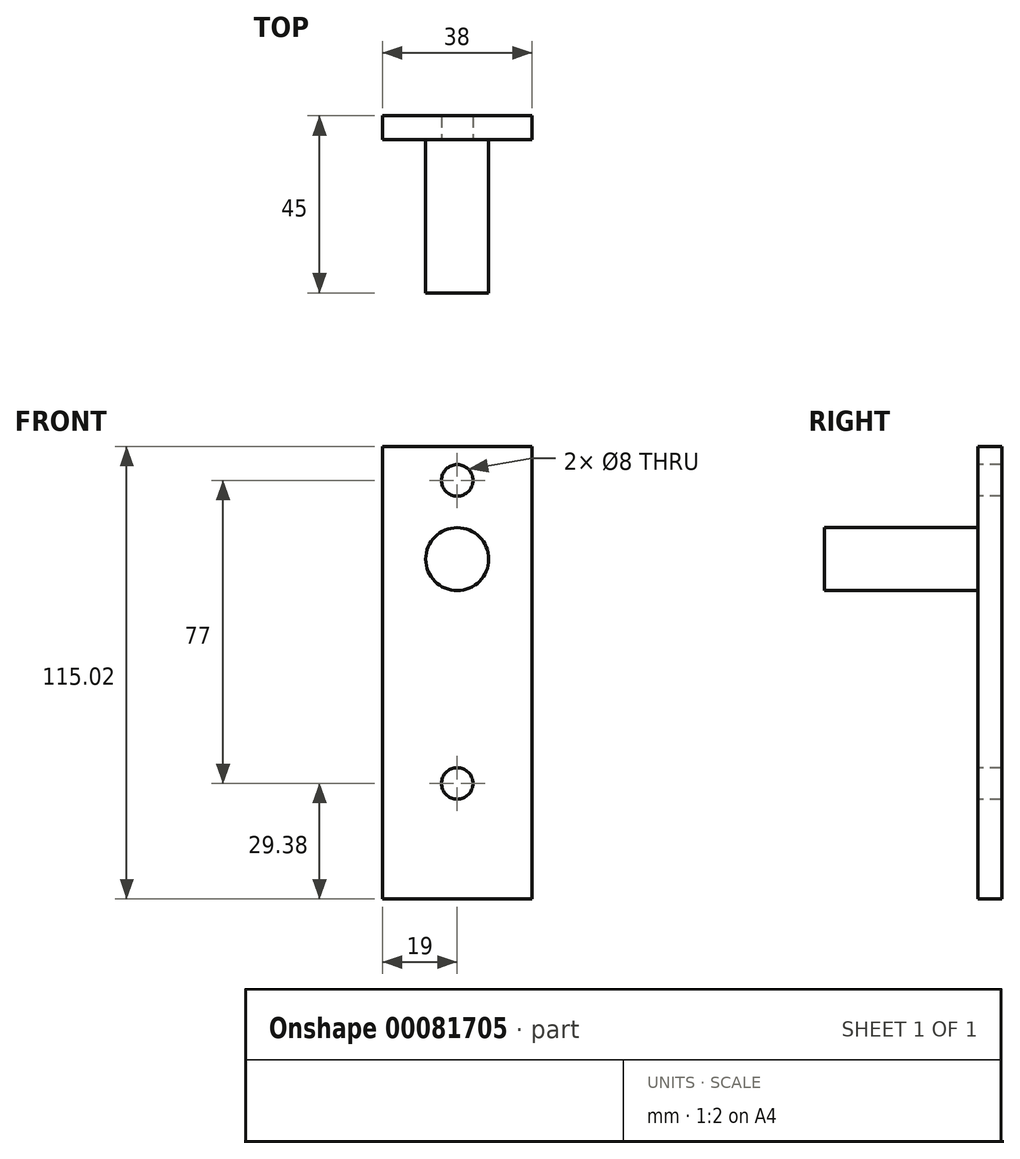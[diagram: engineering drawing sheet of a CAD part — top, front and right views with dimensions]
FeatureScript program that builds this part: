
annotation { "Feature Type Name" : "Feature", "Feature Type Description" : "" }
export const myFeature = defineFeature(function(context is Context, id is Id, definition is map)
    precondition{}
    {
        {
            var Q0;
            Q0=qCreatedBy(makeId("Front.planeOp"),FACE);
            var sketch = newSketch(context, id + "F0", { "sketchPlane" : qUnion([Q0])});
            skLineSegment(sketch, "E0.bottom", {"start": v(19, 57.5) * mm, "end": v(-19, 57.5) * mm});
            skLineSegment(sketch, "E0.top", {"start": v(19, -57.5) * mm, "end": v(-19, -57.5) * mm});
            skLineSegment(sketch, "E0.left", {"start": v(19, 57.5) * mm, "end": v(19, -57.5) * mm});
            skLineSegment(sketch, "E0.right", {"start": v(-19, 57.5) * mm, "end": v(-19, -57.5) * mm});
            skPoint(sketch, "E0.middle", {"position": v(0, 0) * mm});
            skPoint(sketch, "E1.startSnap0", {"position": v(0, 57.5) * mm});
            skCircle(sketch, "E2", {"center": v(0, 28.87) * mm, "radius": 8 * mm});
            skPoint(sketch, "E3.start.orphan", {"position": v(-8, 28.87) * mm});
            skSolve(sketch);
        }
        {
            var Q0;
            Q0 = qSketchRegion(id + "F0", true);
            extrude(context, id + "F1", {"entities" : qUnion([Q0]), "depth" : 6 * mm});
        }
        {
            var Q0;
            Q0=makeQuery(id+"F0.imprint","IMPRINT",FACE,{"disambiguationData":[TD([[makeQuery(id+"F0.imprint","IMPRINT",EDGE,{"derivedFrom":sQuery(id+"F0.wireOp",EDGE,"E2")}),1.0]])]});
            extrude(context, id + "F2", {"entities" : qUnion([Q0]), "operationType" : NewBodyOperationType.ADD, "depth" : 45 * mm});
        }
        {
            var Q0;
            Q0=makeQuery(id+"F1.opExtrude","CAP_FACE",FACE,{"disambiguationData":[OSD([sQuery(id+"F0.wireOp",EDGE,"E0.bottom"),sQuery(id+"F0.wireOp",EDGE,"E0.top"),sQuery(id+"F0.wireOp",EDGE,"E0.left"),sQuery(id+"F0.wireOp",EDGE,"E0.right"),sQuery(id+"F0.wireOp",EDGE,"E2")])],"isStart":false});
            var sketch = newSketch(context, id + "F3", { "sketchPlane" : qUnion([Q0])});
            skCircle(sketch, "E4", {"center": v(0, 48.87) * mm, "radius": 4 * mm});
            skCircle(sketch, "E5", {"center": v(0, -28.13) * mm, "radius": 4 * mm});
            skSolve(sketch);
        }
        {
            var Q0;
            Q0 = qSketchRegion(id + "F3", true);
            extrude(context, id + "F4", {"entities" : qUnion([Q0]), "operationType" : NewBodyOperationType.REMOVE, "endBound" : BoundingType.THROUGH_ALL, "oppositeDirection" : true, "depth" : 25.4 * mm});
        }
    });
